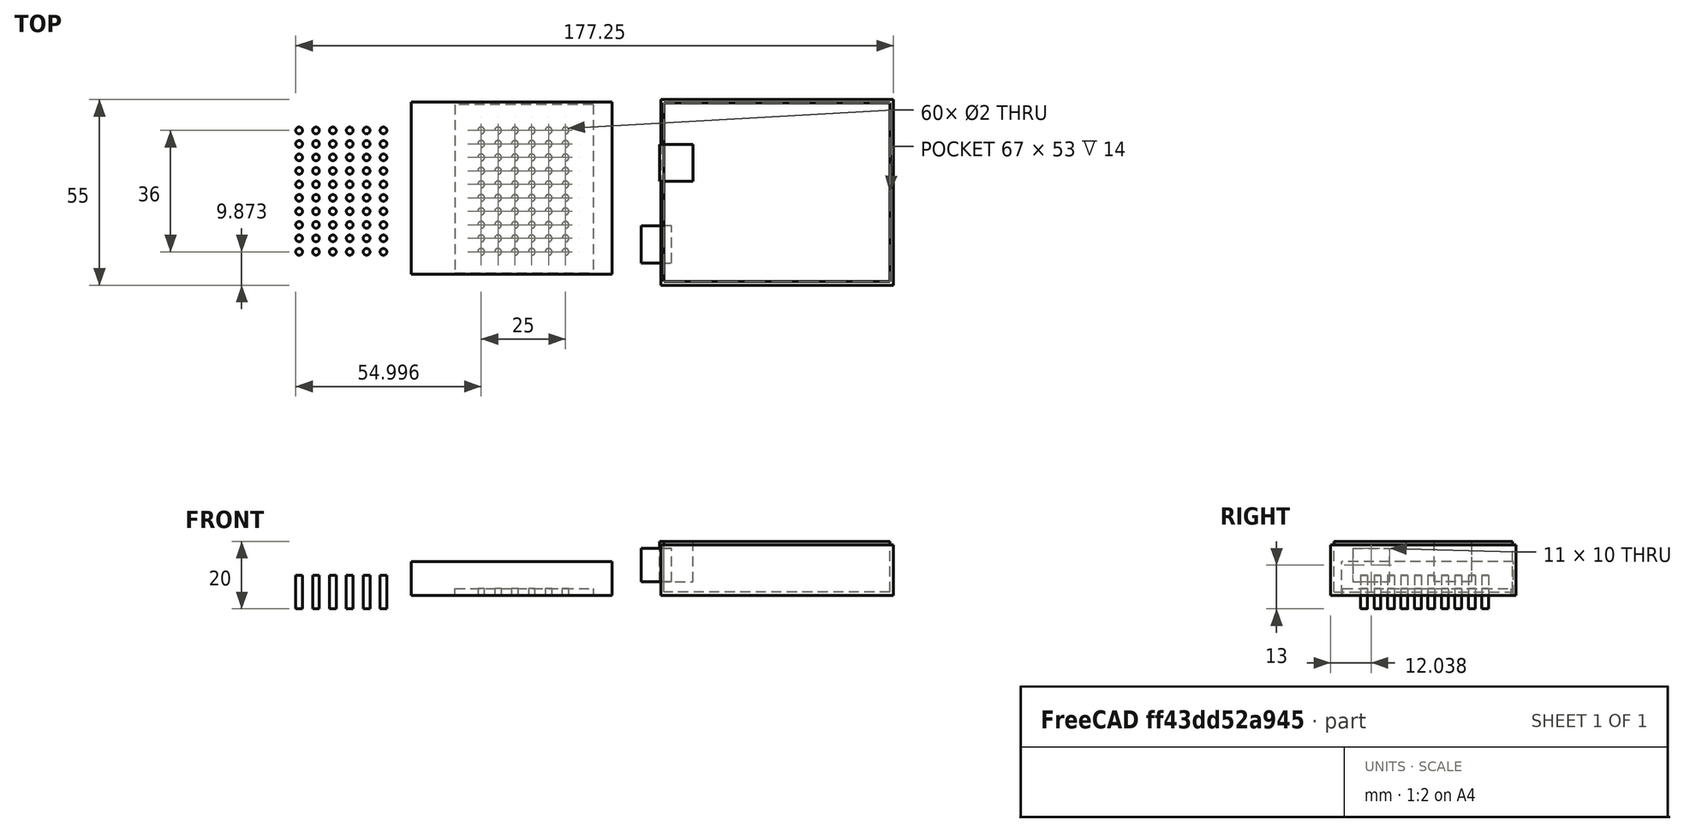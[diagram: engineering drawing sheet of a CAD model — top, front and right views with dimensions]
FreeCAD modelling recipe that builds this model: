
FCSTD DOCUMENT  (FreeCAD 1.0R39109 (Git))
Label: Arduino_component
License: All rights reserved
LicenseURL: https://en.wikipedia.org/wiki/All_rights_reserved
objects: Sketcher::SketchObject×67, PartDesign::Pad×67, PartDesign::Body×67, PartDesign::Boolean×14, Mesh::Feature×1
note: 430 computed .brp shape members not serialized (recipe doc carries the construction recipe); baked Part::Feature solids carry a one-line shape summary decoded from their .brp

FEATURE [Mesh::Feature] arduino
  Placement = pos=(2,0,-5) rot=(0,0,1;0rad)
FEATURE [Sketcher::SketchObject] Sketch
  ArcFitTolerance = 1e-06
  AttachmentSupport = -> [XY_Plane]
  FullyConstrained = false
  MakeInternals = false
  MapMode = 5
  sketch-geometry (4):
    g0: LineSegment StartX=37.3651 StartY=-26.7515 StartZ=0 EndX=-31.6349 EndY=-26.7515 EndZ=0
    g1: LineSegment StartX=-31.6349 StartY=-26.7515 StartZ=0 EndX=-31.6349 EndY=28.2485 EndZ=0
    g2: LineSegment StartX=-31.6349 StartY=28.2485 StartZ=0 EndX=37.3651 EndY=28.2485 EndZ=0
    g3: LineSegment StartX=37.3651 StartY=28.2485 StartZ=0 EndX=37.3651 EndY=-26.7515 EndZ=0
  constraints (10):
    c: Distance(g0) = 69
    c: Horizontal(g0)
    c: Distance(g1) = 55
    c: Coincident(g1,g0)
    c: Vertical(g1)
    c: Distance(g2) = 69
    c: Coincident(g2,g1)
    c: Horizontal(g2)
    c: Coincident(g3,g2)
    c: Coincident(g3,g0)
FEATURE [PartDesign::Pad] Pad
  Direction = (0,0,1)
  Length = 15
  Length2 = 10
  Profile = -> Sketch
  ReferenceAxis = -> Sketch [N_Axis]
  Refine = true
  Suppressed = false
  Type = 0
FEATURE [Sketcher::SketchObject] Sketch001
  ArcFitTolerance = 1e-06
  AttachmentSupport = -> [XY_Plane001]
  FullyConstrained = false
  MakeInternals = false
  MapMode = 5
  sketch-geometry (4):
    g0: LineSegment StartX=6.33937 StartY=-84.733 StartZ=0 EndX=-60.6606 EndY=-84.733 EndZ=0
    g1: LineSegment StartX=-60.6606 StartY=-84.733 StartZ=0 EndX=-60.6606 EndY=-31.733 EndZ=0
    g2: LineSegment StartX=-60.6606 StartY=-31.733 StartZ=0 EndX=6.33937 EndY=-31.733 EndZ=0
    g3: LineSegment StartX=6.33937 StartY=-31.733 StartZ=0 EndX=6.33937 EndY=-84.733 EndZ=0
  constraints (10):
    c: Distance(g0) = 67
    c: Horizontal(g0)
    c: Distance(g1) = 53
    c: Coincident(g1,g0)
    c: Vertical(g1)
    c: Distance(g2) = 67
    c: Coincident(g2,g1)
    c: Horizontal(g2)
    c: Coincident(g3,g2)
    c: Coincident(g3,g0)
FEATURE [PartDesign::Pad] Pad001
  Direction = (0,0,1)
  Length = 15
  Length2 = 10
  Profile = -> Sketch001
  ReferenceAxis = -> Sketch001 [N_Axis]
  Refine = true
  Suppressed = false
  Type = 0
FEATURE [PartDesign::Body] Body001
  AllowCompound = false
  Group = -> [Sketch001,Pad001]
  Origin = -> Origin001
  Placement = pos=(30,59,1) rot=(0,0,1;0rad)
  Tip = -> Pad001
FEATURE [PartDesign::Boolean] Boolean
  BaseFeature = -> Pad
  Group = -> [Body001]
  Refine = true
  Suppressed = false
  Type = 1
  UsePlacement = true
FEATURE [Sketcher::SketchObject] Sketch002
  ArcFitTolerance = 1e-06
  AttachmentSupport = -> [YZ_Plane002]
  FullyConstrained = true
  MakeInternals = false
  MapMode = 5
  Placement = pos=(0,0,0) rot=(0.57735,0.57735,0.57735;2.0944rad)
  sketch-geometry (4):
    g0: LineSegment StartX=11 StartY=0 StartZ=0 EndX=0 EndY=0 EndZ=0
    g1: LineSegment StartX=0 StartY=0 StartZ=0 EndX=0 EndY=12 EndZ=0
    g2: LineSegment StartX=0 StartY=12 StartZ=0 EndX=11 EndY=12 EndZ=0
    g3: LineSegment StartX=11 StartY=12 StartZ=0 EndX=11 EndY=0 EndZ=0
  constraints (11):
    c: Distance(g0) = 11
    c: PointOnObject(g0,g-1)
    c: Coincident(g0,g-1)
    c: Distance(g1) = 12
    c: Coincident(g1,g0)
    c: PointOnObject(g1,g-2)
    c: Distance(g2) = 11
    c: Coincident(g2,g1)
    c: Horizontal(g2)
    c: Coincident(g3,g2)
    c: Coincident(g3,g0)
FEATURE [PartDesign::Pad] Pad002
  Direction = (1,0,0)
  Length = 10
  Length2 = 10
  Placement = pos=(0,0,0) rot=(1,1,1;2.0944rad)
  Profile = -> Sketch002
  ReferenceAxis = -> Sketch002 [N_Axis]
  Refine = true
  Suppressed = false
  Type = 0
FEATURE [PartDesign::Body] Body002
  AllowCompound = false
  Group = -> [Sketch002,Pad002]
  Origin = -> Origin002
  Placement = pos=(-32,4,4) rot=(0,0,1;0rad)
  Tip = -> Pad002
FEATURE [PartDesign::Boolean] Boolean001
  BaseFeature = -> Boolean
  Group = -> [Body002]
  Refine = true
  Suppressed = false
  Type = 1
  UsePlacement = true
FEATURE [Sketcher::SketchObject] Sketch003
  ArcFitTolerance = 1e-06
  AttachmentSupport = -> [XY_Plane003]
  FullyConstrained = false
  MakeInternals = false
  MapMode = 5
  sketch-geometry (4):
    g0: LineSegment StartX=-46.405 StartY=-18.212 StartZ=0 EndX=-37.405 EndY=-18.212 EndZ=0
    g1: LineSegment StartX=-37.405 StartY=-18.212 StartZ=0 EndX=-37.405 EndY=-7.21195 EndZ=0
    g2: LineSegment StartX=-37.405 StartY=-7.21195 StartZ=0 EndX=-46.405 EndY=-7.21195 EndZ=0
    g3: LineSegment StartX=-46.405 StartY=-7.21195 StartZ=0 EndX=-46.405 EndY=-18.212 EndZ=0
  constraints (10):
    c: Distance(g0) = 9
    c: Horizontal(g0)
    c: Distance(g1) = 11
    c: Coincident(g1,g0)
    c: Vertical(g1)
    c: Distance(g2) = 9
    c: Coincident(g2,g1)
    c: Horizontal(g2)
    c: Coincident(g3,g2)
    c: Coincident(g3,g0)
FEATURE [PartDesign::Pad] Pad003
  Direction = (0,0,1)
  Length = 10
  Length2 = 10
  Profile = -> Sketch003
  ReferenceAxis = -> Sketch003 [N_Axis]
  Refine = true
  Suppressed = false
  Type = 0
FEATURE [PartDesign::Body] Body003
  AllowCompound = false
  Group = -> [Sketch003,Pad003]
  Origin = -> Origin003
  Placement = pos=(9,-2,4) rot=(0,0,1;0rad)
  Tip = -> Pad003
FEATURE [PartDesign::Boolean] Boolean002
  BaseFeature = -> Boolean001
  Group = -> [Body003]
  Refine = true
  Suppressed = false
  Type = 1
  UsePlacement = true
FEATURE [PartDesign::Body] Body
  AllowCompound = false
  Group = -> [Sketch,Pad,Boolean,Boolean001,Boolean002]
  Origin = -> Origin
  Tip = -> Boolean002
FEATURE [Sketcher::SketchObject] Sketch004
  ArcFitTolerance = 1e-06
  AttachmentSupport = -> [XY_Plane004]
  FullyConstrained = false
  MakeInternals = false
  MapMode = 5
  sketch-geometry (4):
    g0: LineSegment StartX=-146.689 StartY=-23.1625 StartZ=0 EndX=-46.6885 EndY=-23.1625 EndZ=0
    g1: LineSegment StartX=-46.6885 StartY=-23.1625 StartZ=0 EndX=-46.6885 EndY=26.8375 EndZ=0
    g2: LineSegment StartX=-46.6885 StartY=26.8375 StartZ=0 EndX=-146.689 EndY=26.8375 EndZ=0
    g3: LineSegment StartX=-146.689 StartY=26.8375 StartZ=0 EndX=-146.689 EndY=-23.1625 EndZ=0
  constraints (10):
    c: Distance(g0) = 100
    c: Horizontal(g0)
    c: Distance(g1) = 50
    c: Coincident(g1,g0)
    c: Vertical(g1)
    c: Distance(g2) = 100
    c: Coincident(g2,g1)
    c: Horizontal(g2)
    c: Coincident(g3,g2)
    c: Coincident(g3,g0)
FEATURE [PartDesign::Pad] Pad004
  Direction = (0,0,1)
  Length = 2
  Length2 = 10
  Profile = -> Sketch004
  ReferenceAxis = -> Sketch004 [N_Axis]
  Refine = true
  Suppressed = false
  Type = 0
FEATURE [Sketcher::SketchObject] Sketch005
  ArcFitTolerance = 1e-06
  AttachmentSupport = -> [XY_Plane005]
  FullyConstrained = false
  MakeInternals = false
  MapMode = 5
  sketch-geometry (1):
    g0: Circle CenterX=-36.8843 CenterY=-31.8769 CenterZ=0 NormalX=0 NormalY=0 NormalZ=1 AngleXU=0 Radius=1
  constraints (1):
    c: Diameter(g0) = 2
FEATURE [PartDesign::Pad] Pad005
  Direction = (0,0,1)
  Length = 10
  Length2 = 10
  Profile = -> Sketch005
  ReferenceAxis = -> Sketch005 [N_Axis]
  Refine = true
  Suppressed = false
  Type = 0
FEATURE [PartDesign::Body] Body005
  AllowCompound = false
  Group = -> [Sketch005,Pad005]
  Origin = -> Origin005
  Placement = pos=(-102,15,-4) rot=(0,0,1;0rad)
  Tip = -> Pad005
FEATURE [Sketcher::SketchObject] Sketch006
  ArcFitTolerance = 1e-06
  AttachmentSupport = -> [XY_Plane006]
  FullyConstrained = false
  MakeInternals = false
  MapMode = 5
  sketch-geometry (1):
    g0: Circle CenterX=-36.8843 CenterY=-31.8769 CenterZ=0 NormalX=0 NormalY=0 NormalZ=1 AngleXU=0 Radius=1
  constraints (1):
    c: Diameter(g0) = 2
FEATURE [PartDesign::Pad] Pad006
  Direction = (0,0,1)
  Length = 10
  Length2 = 10
  Profile = -> Sketch006
  ReferenceAxis = -> Sketch006 [N_Axis]
  Refine = true
  Suppressed = false
  Type = 0
FEATURE [PartDesign::Body] Body006
  AllowCompound = false
  Group = -> [Sketch006,Pad006]
  Origin = -> Origin006
  Placement = pos=(-97,15,-4) rot=(0,0,1;0rad)
  Tip = -> Pad006
FEATURE [Sketcher::SketchObject] Sketch007
  ArcFitTolerance = 1e-06
  AttachmentSupport = -> [XY_Plane007]
  FullyConstrained = false
  MakeInternals = false
  MapMode = 5
  sketch-geometry (1):
    g0: Circle CenterX=-36.8843 CenterY=-31.8769 CenterZ=0 NormalX=0 NormalY=0 NormalZ=1 AngleXU=0 Radius=1
  constraints (1):
    c: Diameter(g0) = 2
FEATURE [PartDesign::Pad] Pad007
  Direction = (0,0,1)
  Length = 10
  Length2 = 10
  Profile = -> Sketch007
  ReferenceAxis = -> Sketch007 [N_Axis]
  Refine = true
  Suppressed = false
  Type = 0
FEATURE [PartDesign::Body] Body007
  AllowCompound = false
  Group = -> [Sketch007,Pad007]
  Origin = -> Origin007
  Placement = pos=(-92,15,-4) rot=(0,0,1;0rad)
  Tip = -> Pad007
FEATURE [Sketcher::SketchObject] Sketch008
  ArcFitTolerance = 1e-06
  AttachmentSupport = -> [XY_Plane008]
  FullyConstrained = false
  MakeInternals = false
  MapMode = 5
  sketch-geometry (1):
    g0: Circle CenterX=-36.8843 CenterY=-31.8769 CenterZ=0 NormalX=0 NormalY=0 NormalZ=1 AngleXU=0 Radius=1
  constraints (1):
    c: Diameter(g0) = 2
FEATURE [PartDesign::Pad] Pad008
  Direction = (0,0,1)
  Length = 10
  Length2 = 10
  Profile = -> Sketch008
  ReferenceAxis = -> Sketch008 [N_Axis]
  Refine = true
  Suppressed = false
  Type = 0
FEATURE [PartDesign::Body] Body008
  AllowCompound = false
  Group = -> [Sketch008,Pad008]
  Origin = -> Origin008
  Placement = pos=(-87,15,-4) rot=(0,0,1;0rad)
  Tip = -> Pad008
FEATURE [Sketcher::SketchObject] Sketch009
  ArcFitTolerance = 1e-06
  AttachmentSupport = -> [XY_Plane009]
  FullyConstrained = false
  MakeInternals = false
  MapMode = 5
  sketch-geometry (1):
    g0: Circle CenterX=-36.8843 CenterY=-31.8769 CenterZ=0 NormalX=0 NormalY=0 NormalZ=1 AngleXU=0 Radius=1
  constraints (1):
    c: Diameter(g0) = 2
FEATURE [PartDesign::Pad] Pad009
  Direction = (0,0,1)
  Length = 10
  Length2 = 10
  Profile = -> Sketch009
  ReferenceAxis = -> Sketch009 [N_Axis]
  Refine = true
  Suppressed = false
  Type = 0
FEATURE [PartDesign::Body] Body009
  AllowCompound = false
  Group = -> [Sketch009,Pad009]
  Origin = -> Origin009
  Placement = pos=(-82,15,-4) rot=(0,0,1;0rad)
  Tip = -> Pad009
FEATURE [Sketcher::SketchObject] Sketch010
  ArcFitTolerance = 1e-06
  AttachmentSupport = -> [XY_Plane010]
  FullyConstrained = false
  MakeInternals = false
  MapMode = 5
  sketch-geometry (1):
    g0: Circle CenterX=-36.8843 CenterY=-31.8769 CenterZ=0 NormalX=0 NormalY=0 NormalZ=1 AngleXU=0 Radius=1
  constraints (1):
    c: Diameter(g0) = 2
FEATURE [PartDesign::Pad] Pad010
  Direction = (0,0,1)
  Length = 10
  Length2 = 10
  Profile = -> Sketch010
  ReferenceAxis = -> Sketch010 [N_Axis]
  Refine = true
  Suppressed = false
  Type = 0
FEATURE [PartDesign::Body] Body010
  AllowCompound = false
  Group = -> [Sketch010,Pad010]
  Origin = -> Origin010
  Placement = pos=(-77,15,-4) rot=(0,0,1;0rad)
  Tip = -> Pad010
FEATURE [PartDesign::Boolean] Boolean003
  BaseFeature = -> Pad004
  Group = -> [Body005,Body006,Body007,Body008,Body009]
  Refine = true
  Suppressed = false
  Type = 1
  UsePlacement = true
FEATURE [Sketcher::SketchObject] Sketch011
  ArcFitTolerance = 1e-06
  AttachmentSupport = -> [XY_Plane011]
  FullyConstrained = false
  MakeInternals = false
  MapMode = 5
  sketch-geometry (1):
    g0: Circle CenterX=-36.8843 CenterY=-31.8769 CenterZ=0 NormalX=0 NormalY=0 NormalZ=1 AngleXU=0 Radius=1
  constraints (1):
    c: Diameter(g0) = 2
FEATURE [PartDesign::Pad] Pad011
  Direction = (0,0,1)
  Length = 10
  Length2 = 10
  Profile = -> Sketch011
  ReferenceAxis = -> Sketch011 [N_Axis]
  Refine = true
  Suppressed = false
  Type = 0
FEATURE [PartDesign::Body] Body011
  AllowCompound = false
  Group = -> [Sketch011,Pad011]
  Origin = -> Origin011
  Placement = pos=(-102,19,-4) rot=(0,0,1;0rad)
  Tip = -> Pad011
FEATURE [Sketcher::SketchObject] Sketch012
  ArcFitTolerance = 1e-06
  AttachmentSupport = -> [XY_Plane012]
  FullyConstrained = false
  MakeInternals = false
  MapMode = 5
  sketch-geometry (1):
    g0: Circle CenterX=-36.8843 CenterY=-31.8769 CenterZ=0 NormalX=0 NormalY=0 NormalZ=1 AngleXU=0 Radius=1
  constraints (1):
    c: Diameter(g0) = 2
FEATURE [PartDesign::Pad] Pad012
  Direction = (0,0,1)
  Length = 10
  Length2 = 10
  Profile = -> Sketch012
  ReferenceAxis = -> Sketch012 [N_Axis]
  Refine = true
  Suppressed = false
  Type = 0
FEATURE [PartDesign::Body] Body012
  AllowCompound = false
  Group = -> [Sketch012,Pad012]
  Origin = -> Origin012
  Placement = pos=(-97,19,-4) rot=(0,0,1;0rad)
  Tip = -> Pad012
FEATURE [Sketcher::SketchObject] Sketch013
  ArcFitTolerance = 1e-06
  AttachmentSupport = -> [XY_Plane013]
  FullyConstrained = false
  MakeInternals = false
  MapMode = 5
  sketch-geometry (1):
    g0: Circle CenterX=-36.8843 CenterY=-31.8769 CenterZ=0 NormalX=0 NormalY=0 NormalZ=1 AngleXU=0 Radius=1
  constraints (1):
    c: Diameter(g0) = 2
FEATURE [PartDesign::Pad] Pad013
  Direction = (0,0,1)
  Length = 10
  Length2 = 10
  Profile = -> Sketch013
  ReferenceAxis = -> Sketch013 [N_Axis]
  Refine = true
  Suppressed = false
  Type = 0
FEATURE [PartDesign::Body] Body013
  AllowCompound = false
  Group = -> [Sketch013,Pad013]
  Origin = -> Origin013
  Placement = pos=(-92,19,-4) rot=(0,0,1;0rad)
  Tip = -> Pad013
FEATURE [Sketcher::SketchObject] Sketch014
  ArcFitTolerance = 1e-06
  AttachmentSupport = -> [XY_Plane014]
  FullyConstrained = false
  MakeInternals = false
  MapMode = 5
  sketch-geometry (1):
    g0: Circle CenterX=-36.8843 CenterY=-31.8769 CenterZ=0 NormalX=0 NormalY=0 NormalZ=1 AngleXU=0 Radius=1
  constraints (1):
    c: Diameter(g0) = 2
FEATURE [PartDesign::Pad] Pad014
  Direction = (0,0,1)
  Length = 10
  Length2 = 10
  Profile = -> Sketch014
  ReferenceAxis = -> Sketch014 [N_Axis]
  Refine = true
  Suppressed = false
  Type = 0
FEATURE [PartDesign::Body] Body014
  AllowCompound = false
  Group = -> [Sketch014,Pad014]
  Origin = -> Origin014
  Placement = pos=(-87,19,-4) rot=(0,0,1;0rad)
  Tip = -> Pad014
FEATURE [Sketcher::SketchObject] Sketch015
  ArcFitTolerance = 1e-06
  AttachmentSupport = -> [XY_Plane015]
  FullyConstrained = false
  MakeInternals = false
  MapMode = 5
  sketch-geometry (1):
    g0: Circle CenterX=-36.8843 CenterY=-31.8769 CenterZ=0 NormalX=0 NormalY=0 NormalZ=1 AngleXU=0 Radius=1
  constraints (1):
    c: Diameter(g0) = 2
FEATURE [PartDesign::Pad] Pad015
  Direction = (0,0,1)
  Length = 10
  Length2 = 10
  Profile = -> Sketch015
  ReferenceAxis = -> Sketch015 [N_Axis]
  Refine = true
  Suppressed = false
  Type = 0
FEATURE [PartDesign::Body] Body015
  AllowCompound = false
  Group = -> [Sketch015,Pad015]
  Origin = -> Origin015
  Placement = pos=(-82,19,-4) rot=(0,0,1;0rad)
  Tip = -> Pad015
FEATURE [Sketcher::SketchObject] Sketch016
  ArcFitTolerance = 1e-06
  AttachmentSupport = -> [XY_Plane016]
  FullyConstrained = false
  MakeInternals = false
  MapMode = 5
  sketch-geometry (1):
    g0: Circle CenterX=-36.8843 CenterY=-31.8769 CenterZ=0 NormalX=0 NormalY=0 NormalZ=1 AngleXU=0 Radius=1
  constraints (1):
    c: Diameter(g0) = 2
FEATURE [PartDesign::Pad] Pad016
  Direction = (0,0,1)
  Length = 10
  Length2 = 10
  Profile = -> Sketch016
  ReferenceAxis = -> Sketch016 [N_Axis]
  Refine = true
  Suppressed = false
  Type = 0
FEATURE [PartDesign::Body] Body016
  AllowCompound = false
  Group = -> [Sketch016,Pad016]
  Origin = -> Origin016
  Placement = pos=(-77,19,-4) rot=(0,0,1;0rad)
  Tip = -> Pad016
FEATURE [Sketcher::SketchObject] Sketch017
  ArcFitTolerance = 1e-06
  AttachmentSupport = -> [XY_Plane017]
  FullyConstrained = false
  MakeInternals = false
  MapMode = 5
  sketch-geometry (1):
    g0: Circle CenterX=-36.8843 CenterY=-31.8769 CenterZ=0 NormalX=0 NormalY=0 NormalZ=1 AngleXU=0 Radius=1
  constraints (1):
    c: Diameter(g0) = 2
FEATURE [PartDesign::Pad] Pad017
  Direction = (0,0,1)
  Length = 10
  Length2 = 10
  Profile = -> Sketch017
  ReferenceAxis = -> Sketch017 [N_Axis]
  Refine = true
  Suppressed = false
  Type = 0
FEATURE [PartDesign::Body] Body017
  AllowCompound = false
  Group = -> [Sketch017,Pad017]
  Origin = -> Origin017
  Placement = pos=(-77,15,-4) rot=(0,0,1;0rad)
  Tip = -> Pad017
FEATURE [PartDesign::Boolean] Boolean004
  BaseFeature = -> Boolean003
  Group = -> [Body011,Body012,Body013,Body014,Body015,Body016,Body017,Body010]
  Refine = true
  Suppressed = false
  Type = 1
  UsePlacement = true
FEATURE [Sketcher::SketchObject] Sketch018
  ArcFitTolerance = 1e-06
  AttachmentSupport = -> [XY_Plane018]
  FullyConstrained = false
  MakeInternals = false
  MapMode = 5
  sketch-geometry (1):
    g0: Circle CenterX=-36.8843 CenterY=-31.8769 CenterZ=0 NormalX=0 NormalY=0 NormalZ=1 AngleXU=0 Radius=1
  constraints (1):
    c: Diameter(g0) = 2
FEATURE [PartDesign::Pad] Pad018
  Direction = (0,0,1)
  Length = 10
  Length2 = 10
  Profile = -> Sketch018
  ReferenceAxis = -> Sketch018 [N_Axis]
  Refine = true
  Suppressed = false
  Type = 0
FEATURE [PartDesign::Body] Body018
  AllowCompound = false
  Group = -> [Sketch018,Pad018]
  Origin = -> Origin018
  Placement = pos=(-102,23,-4) rot=(0,0,1;0rad)
  Tip = -> Pad018
FEATURE [Sketcher::SketchObject] Sketch019
  ArcFitTolerance = 1e-06
  AttachmentSupport = -> [XY_Plane019]
  FullyConstrained = false
  MakeInternals = false
  MapMode = 5
  sketch-geometry (1):
    g0: Circle CenterX=-36.8843 CenterY=-31.8769 CenterZ=0 NormalX=0 NormalY=0 NormalZ=1 AngleXU=0 Radius=1
  constraints (1):
    c: Diameter(g0) = 2
FEATURE [PartDesign::Pad] Pad019
  Direction = (0,0,1)
  Length = 10
  Length2 = 10
  Profile = -> Sketch019
  ReferenceAxis = -> Sketch019 [N_Axis]
  Refine = true
  Suppressed = false
  Type = 0
FEATURE [PartDesign::Body] Body019
  AllowCompound = false
  Group = -> [Sketch019,Pad019]
  Origin = -> Origin019
  Placement = pos=(-97,23,-4) rot=(0,0,1;0rad)
  Tip = -> Pad019
FEATURE [Sketcher::SketchObject] Sketch020
  ArcFitTolerance = 1e-06
  AttachmentSupport = -> [XY_Plane020]
  FullyConstrained = false
  MakeInternals = false
  MapMode = 5
  sketch-geometry (1):
    g0: Circle CenterX=-36.8843 CenterY=-31.8769 CenterZ=0 NormalX=0 NormalY=0 NormalZ=1 AngleXU=0 Radius=1
  constraints (1):
    c: Diameter(g0) = 2
FEATURE [PartDesign::Pad] Pad020
  Direction = (0,0,1)
  Length = 10
  Length2 = 10
  Profile = -> Sketch020
  ReferenceAxis = -> Sketch020 [N_Axis]
  Refine = true
  Suppressed = false
  Type = 0
FEATURE [PartDesign::Body] Body020
  AllowCompound = false
  Group = -> [Sketch020,Pad020]
  Origin = -> Origin020
  Placement = pos=(-92,23,-4) rot=(0,0,1;0rad)
  Tip = -> Pad020
FEATURE [Sketcher::SketchObject] Sketch021
  ArcFitTolerance = 1e-06
  AttachmentSupport = -> [XY_Plane021]
  FullyConstrained = false
  MakeInternals = false
  MapMode = 5
  sketch-geometry (1):
    g0: Circle CenterX=-36.8843 CenterY=-31.8769 CenterZ=0 NormalX=0 NormalY=0 NormalZ=1 AngleXU=0 Radius=1
  constraints (1):
    c: Diameter(g0) = 2
FEATURE [PartDesign::Pad] Pad021
  Direction = (0,0,1)
  Length = 10
  Length2 = 10
  Profile = -> Sketch021
  ReferenceAxis = -> Sketch021 [N_Axis]
  Refine = true
  Suppressed = false
  Type = 0
FEATURE [PartDesign::Body] Body021
  AllowCompound = false
  Group = -> [Sketch021,Pad021]
  Origin = -> Origin021
  Placement = pos=(-87,23,-4) rot=(0,0,1;0rad)
  Tip = -> Pad021
FEATURE [Sketcher::SketchObject] Sketch022
  ArcFitTolerance = 1e-06
  AttachmentSupport = -> [XY_Plane022]
  FullyConstrained = false
  MakeInternals = false
  MapMode = 5
  sketch-geometry (1):
    g0: Circle CenterX=-36.8843 CenterY=-31.8769 CenterZ=0 NormalX=0 NormalY=0 NormalZ=1 AngleXU=0 Radius=1
  constraints (1):
    c: Diameter(g0) = 2
FEATURE [PartDesign::Pad] Pad022
  Direction = (0,0,1)
  Length = 10
  Length2 = 10
  Profile = -> Sketch022
  ReferenceAxis = -> Sketch022 [N_Axis]
  Refine = true
  Suppressed = false
  Type = 0
FEATURE [PartDesign::Body] Body022
  AllowCompound = false
  Group = -> [Sketch022,Pad022]
  Origin = -> Origin022
  Placement = pos=(-82,23,-4) rot=(0,0,1;0rad)
  Tip = -> Pad022
FEATURE [Sketcher::SketchObject] Sketch023
  ArcFitTolerance = 1e-06
  AttachmentSupport = -> [XY_Plane023]
  FullyConstrained = false
  MakeInternals = false
  MapMode = 5
  sketch-geometry (1):
    g0: Circle CenterX=-36.8843 CenterY=-31.8769 CenterZ=0 NormalX=0 NormalY=0 NormalZ=1 AngleXU=0 Radius=1
  constraints (1):
    c: Diameter(g0) = 2
FEATURE [PartDesign::Pad] Pad023
  Direction = (0,0,1)
  Length = 10
  Length2 = 10
  Profile = -> Sketch023
  ReferenceAxis = -> Sketch023 [N_Axis]
  Refine = true
  Suppressed = false
  Type = 0
FEATURE [PartDesign::Body] Body023
  AllowCompound = false
  Group = -> [Sketch023,Pad023]
  Origin = -> Origin023
  Placement = pos=(-77,23,-4) rot=(0,0,1;0rad)
  Tip = -> Pad023
FEATURE [PartDesign::Boolean] Boolean005
  BaseFeature = -> Boolean004
  Group = -> [Body018,Body019,Body020,Body021,Body022,Body023]
  Refine = true
  Suppressed = false
  Type = 1
  UsePlacement = true
FEATURE [Sketcher::SketchObject] Sketch024
  ArcFitTolerance = 1e-06
  AttachmentSupport = -> [XY_Plane024]
  FullyConstrained = false
  MakeInternals = false
  MapMode = 5
  sketch-geometry (1):
    g0: Circle CenterX=-36.8843 CenterY=-31.8769 CenterZ=0 NormalX=0 NormalY=0 NormalZ=1 AngleXU=0 Radius=1
  constraints (1):
    c: Diameter(g0) = 2
FEATURE [PartDesign::Pad] Pad024
  Direction = (0,0,1)
  Length = 10
  Length2 = 10
  Profile = -> Sketch024
  ReferenceAxis = -> Sketch024 [N_Axis]
  Refine = true
  Suppressed = false
  Type = 0
FEATURE [PartDesign::Body] Body024
  AllowCompound = false
  Group = -> [Sketch024,Pad024]
  Origin = -> Origin024
  Placement = pos=(-102,27,-4) rot=(0,0,1;0rad)
  Tip = -> Pad024
FEATURE [Sketcher::SketchObject] Sketch025
  ArcFitTolerance = 1e-06
  AttachmentSupport = -> [XY_Plane025]
  FullyConstrained = false
  MakeInternals = false
  MapMode = 5
  sketch-geometry (1):
    g0: Circle CenterX=-36.8843 CenterY=-31.8769 CenterZ=0 NormalX=0 NormalY=0 NormalZ=1 AngleXU=0 Radius=1
  constraints (1):
    c: Diameter(g0) = 2
FEATURE [PartDesign::Pad] Pad025
  Direction = (0,0,1)
  Length = 10
  Length2 = 10
  Profile = -> Sketch025
  ReferenceAxis = -> Sketch025 [N_Axis]
  Refine = true
  Suppressed = false
  Type = 0
FEATURE [PartDesign::Body] Body025
  AllowCompound = false
  Group = -> [Sketch025,Pad025]
  Origin = -> Origin025
  Placement = pos=(-97,27,-4) rot=(0,0,1;0rad)
  Tip = -> Pad025
FEATURE [Sketcher::SketchObject] Sketch026
  ArcFitTolerance = 1e-06
  AttachmentSupport = -> [XY_Plane026]
  FullyConstrained = false
  MakeInternals = false
  MapMode = 5
  sketch-geometry (1):
    g0: Circle CenterX=-36.8843 CenterY=-31.8769 CenterZ=0 NormalX=0 NormalY=0 NormalZ=1 AngleXU=0 Radius=1
  constraints (1):
    c: Diameter(g0) = 2
FEATURE [PartDesign::Pad] Pad026
  Direction = (0,0,1)
  Length = 10
  Length2 = 10
  Profile = -> Sketch026
  ReferenceAxis = -> Sketch026 [N_Axis]
  Refine = true
  Suppressed = false
  Type = 0
FEATURE [PartDesign::Body] Body026
  AllowCompound = false
  Group = -> [Sketch026,Pad026]
  Origin = -> Origin026
  Placement = pos=(-92,27,-4) rot=(0,0,1;0rad)
  Tip = -> Pad026
FEATURE [Sketcher::SketchObject] Sketch027
  ArcFitTolerance = 1e-06
  AttachmentSupport = -> [XY_Plane027]
  FullyConstrained = false
  MakeInternals = false
  MapMode = 5
  sketch-geometry (1):
    g0: Circle CenterX=-36.8843 CenterY=-31.8769 CenterZ=0 NormalX=0 NormalY=0 NormalZ=1 AngleXU=0 Radius=1
  constraints (1):
    c: Diameter(g0) = 2
FEATURE [PartDesign::Pad] Pad027
  Direction = (0,0,1)
  Length = 10
  Length2 = 10
  Profile = -> Sketch027
  ReferenceAxis = -> Sketch027 [N_Axis]
  Refine = true
  Suppressed = false
  Type = 0
FEATURE [PartDesign::Body] Body027
  AllowCompound = false
  Group = -> [Sketch027,Pad027]
  Origin = -> Origin027
  Placement = pos=(-87,27,-4) rot=(0,0,1;0rad)
  Tip = -> Pad027
FEATURE [Sketcher::SketchObject] Sketch028
  ArcFitTolerance = 1e-06
  AttachmentSupport = -> [XY_Plane028]
  FullyConstrained = false
  MakeInternals = false
  MapMode = 5
  sketch-geometry (1):
    g0: Circle CenterX=-36.8843 CenterY=-31.8769 CenterZ=0 NormalX=0 NormalY=0 NormalZ=1 AngleXU=0 Radius=1
  constraints (1):
    c: Diameter(g0) = 2
FEATURE [PartDesign::Pad] Pad028
  Direction = (0,0,1)
  Length = 10
  Length2 = 10
  Profile = -> Sketch028
  ReferenceAxis = -> Sketch028 [N_Axis]
  Refine = true
  Suppressed = false
  Type = 0
FEATURE [PartDesign::Body] Body028
  AllowCompound = false
  Group = -> [Sketch028,Pad028]
  Origin = -> Origin028
  Placement = pos=(-82,27,-4) rot=(0,0,1;0rad)
  Tip = -> Pad028
FEATURE [Sketcher::SketchObject] Sketch029
  ArcFitTolerance = 1e-06
  AttachmentSupport = -> [XY_Plane029]
  FullyConstrained = false
  MakeInternals = false
  MapMode = 5
  sketch-geometry (1):
    g0: Circle CenterX=-36.8843 CenterY=-31.8769 CenterZ=0 NormalX=0 NormalY=0 NormalZ=1 AngleXU=0 Radius=1
  constraints (1):
    c: Diameter(g0) = 2
FEATURE [PartDesign::Pad] Pad029
  Direction = (0,0,1)
  Length = 10
  Length2 = 10
  Profile = -> Sketch029
  ReferenceAxis = -> Sketch029 [N_Axis]
  Refine = true
  Suppressed = false
  Type = 0
FEATURE [PartDesign::Body] Body029
  AllowCompound = false
  Group = -> [Sketch029,Pad029]
  Origin = -> Origin029
  Placement = pos=(-77,27,-4) rot=(0,0,1;0rad)
  Tip = -> Pad029
FEATURE [PartDesign::Boolean] Boolean006
  BaseFeature = -> Boolean005
  Group = -> [Body024,Body025,Body026,Body027,Body028,Body029]
  Refine = true
  Suppressed = false
  Type = 1
  UsePlacement = true
FEATURE [Sketcher::SketchObject] Sketch030
  ArcFitTolerance = 1e-06
  AttachmentSupport = -> [XY_Plane030]
  FullyConstrained = false
  MakeInternals = false
  MapMode = 5
  sketch-geometry (1):
    g0: Circle CenterX=-36.8843 CenterY=-31.8769 CenterZ=0 NormalX=0 NormalY=0 NormalZ=1 AngleXU=0 Radius=1
  constraints (1):
    c: Diameter(g0) = 2
FEATURE [PartDesign::Pad] Pad030
  Direction = (0,0,1)
  Length = 10
  Length2 = 10
  Profile = -> Sketch030
  ReferenceAxis = -> Sketch030 [N_Axis]
  Refine = true
  Suppressed = false
  Type = 0
FEATURE [PartDesign::Body] Body030
  AllowCompound = false
  Group = -> [Sketch030,Pad030]
  Origin = -> Origin030
  Placement = pos=(-102,31,-4) rot=(0,0,1;0rad)
  Tip = -> Pad030
FEATURE [Sketcher::SketchObject] Sketch031
  ArcFitTolerance = 1e-06
  AttachmentSupport = -> [XY_Plane031]
  FullyConstrained = false
  MakeInternals = false
  MapMode = 5
  sketch-geometry (1):
    g0: Circle CenterX=-36.8843 CenterY=-31.8769 CenterZ=0 NormalX=0 NormalY=0 NormalZ=1 AngleXU=0 Radius=1
  constraints (1):
    c: Diameter(g0) = 2
FEATURE [PartDesign::Pad] Pad031
  Direction = (0,0,1)
  Length = 10
  Length2 = 10
  Profile = -> Sketch031
  ReferenceAxis = -> Sketch031 [N_Axis]
  Refine = true
  Suppressed = false
  Type = 0
FEATURE [PartDesign::Body] Body031
  AllowCompound = false
  Group = -> [Sketch031,Pad031]
  Origin = -> Origin031
  Placement = pos=(-97,31,-4) rot=(0,0,1;0rad)
  Tip = -> Pad031
FEATURE [Sketcher::SketchObject] Sketch032
  ArcFitTolerance = 1e-06
  AttachmentSupport = -> [XY_Plane032]
  FullyConstrained = false
  MakeInternals = false
  MapMode = 5
  sketch-geometry (1):
    g0: Circle CenterX=-36.8843 CenterY=-31.8769 CenterZ=0 NormalX=0 NormalY=0 NormalZ=1 AngleXU=0 Radius=1
  constraints (1):
    c: Diameter(g0) = 2
FEATURE [PartDesign::Pad] Pad032
  Direction = (0,0,1)
  Length = 10
  Length2 = 10
  Profile = -> Sketch032
  ReferenceAxis = -> Sketch032 [N_Axis]
  Refine = true
  Suppressed = false
  Type = 0
FEATURE [PartDesign::Body] Body032
  AllowCompound = false
  Group = -> [Sketch032,Pad032]
  Origin = -> Origin032
  Placement = pos=(-92,31,-4) rot=(0,0,1;0rad)
  Tip = -> Pad032
FEATURE [Sketcher::SketchObject] Sketch033
  ArcFitTolerance = 1e-06
  AttachmentSupport = -> [XY_Plane033]
  FullyConstrained = false
  MakeInternals = false
  MapMode = 5
  sketch-geometry (1):
    g0: Circle CenterX=-36.8843 CenterY=-31.8769 CenterZ=0 NormalX=0 NormalY=0 NormalZ=1 AngleXU=0 Radius=1
  constraints (1):
    c: Diameter(g0) = 2
FEATURE [PartDesign::Pad] Pad033
  Direction = (0,0,1)
  Length = 10
  Length2 = 10
  Profile = -> Sketch033
  ReferenceAxis = -> Sketch033 [N_Axis]
  Refine = true
  Suppressed = false
  Type = 0
FEATURE [PartDesign::Body] Body033
  AllowCompound = false
  Group = -> [Sketch033,Pad033]
  Origin = -> Origin033
  Placement = pos=(-87,31,-4) rot=(0,0,1;0rad)
  Tip = -> Pad033
FEATURE [Sketcher::SketchObject] Sketch034
  ArcFitTolerance = 1e-06
  AttachmentSupport = -> [XY_Plane034]
  FullyConstrained = false
  MakeInternals = false
  MapMode = 5
  sketch-geometry (1):
    g0: Circle CenterX=-36.8843 CenterY=-31.8769 CenterZ=0 NormalX=0 NormalY=0 NormalZ=1 AngleXU=0 Radius=1
  constraints (1):
    c: Diameter(g0) = 2
FEATURE [PartDesign::Pad] Pad034
  Direction = (0,0,1)
  Length = 10
  Length2 = 10
  Profile = -> Sketch034
  ReferenceAxis = -> Sketch034 [N_Axis]
  Refine = true
  Suppressed = false
  Type = 0
FEATURE [PartDesign::Body] Body034
  AllowCompound = false
  Group = -> [Sketch034,Pad034]
  Origin = -> Origin034
  Placement = pos=(-82,31,-4) rot=(0,0,1;0rad)
  Tip = -> Pad034
FEATURE [Sketcher::SketchObject] Sketch035
  ArcFitTolerance = 1e-06
  AttachmentSupport = -> [XY_Plane035]
  FullyConstrained = false
  MakeInternals = false
  MapMode = 5
  sketch-geometry (1):
    g0: Circle CenterX=-36.8843 CenterY=-31.8769 CenterZ=0 NormalX=0 NormalY=0 NormalZ=1 AngleXU=0 Radius=1
  constraints (1):
    c: Diameter(g0) = 2
FEATURE [PartDesign::Pad] Pad035
  Direction = (0,0,1)
  Length = 10
  Length2 = 10
  Profile = -> Sketch035
  ReferenceAxis = -> Sketch035 [N_Axis]
  Refine = true
  Suppressed = false
  Type = 0
FEATURE [PartDesign::Body] Body035
  AllowCompound = false
  Group = -> [Sketch035,Pad035]
  Origin = -> Origin035
  Placement = pos=(-77,31,-4) rot=(0,0,1;0rad)
  Tip = -> Pad035
FEATURE [PartDesign::Boolean] Boolean007
  BaseFeature = -> Boolean006
  Group = -> [Body030,Body031,Body032,Body033,Body034,Body035]
  Refine = true
  Suppressed = false
  Type = 1
  UsePlacement = true
FEATURE [Sketcher::SketchObject] Sketch036
  ArcFitTolerance = 1e-06
  AttachmentSupport = -> [XY_Plane036]
  FullyConstrained = false
  MakeInternals = false
  MapMode = 5
  sketch-geometry (1):
    g0: Circle CenterX=-36.8843 CenterY=-31.8769 CenterZ=0 NormalX=0 NormalY=0 NormalZ=1 AngleXU=0 Radius=1
  constraints (1):
    c: Diameter(g0) = 2
FEATURE [PartDesign::Pad] Pad036
  Direction = (0,0,1)
  Length = 10
  Length2 = 10
  Profile = -> Sketch036
  ReferenceAxis = -> Sketch036 [N_Axis]
  Refine = true
  Suppressed = false
  Type = 0
FEATURE [PartDesign::Body] Body036
  AllowCompound = false
  Group = -> [Sketch036,Pad036]
  Origin = -> Origin036
  Placement = pos=(-102,35,-4) rot=(0,0,1;0rad)
  Tip = -> Pad036
FEATURE [Sketcher::SketchObject] Sketch037
  ArcFitTolerance = 1e-06
  AttachmentSupport = -> [XY_Plane037]
  FullyConstrained = false
  MakeInternals = false
  MapMode = 5
  sketch-geometry (1):
    g0: Circle CenterX=-36.8843 CenterY=-31.8769 CenterZ=0 NormalX=0 NormalY=0 NormalZ=1 AngleXU=0 Radius=1
  constraints (1):
    c: Diameter(g0) = 2
FEATURE [PartDesign::Pad] Pad037
  Direction = (0,0,1)
  Length = 10
  Length2 = 10
  Profile = -> Sketch037
  ReferenceAxis = -> Sketch037 [N_Axis]
  Refine = true
  Suppressed = false
  Type = 0
FEATURE [PartDesign::Body] Body037
  AllowCompound = false
  Group = -> [Sketch037,Pad037]
  Origin = -> Origin037
  Placement = pos=(-97,35,-4) rot=(0,0,1;0rad)
  Tip = -> Pad037
FEATURE [Sketcher::SketchObject] Sketch038
  ArcFitTolerance = 1e-06
  AttachmentSupport = -> [XY_Plane038]
  FullyConstrained = false
  MakeInternals = false
  MapMode = 5
  sketch-geometry (1):
    g0: Circle CenterX=-36.8843 CenterY=-31.8769 CenterZ=0 NormalX=0 NormalY=0 NormalZ=1 AngleXU=0 Radius=1
  constraints (1):
    c: Diameter(g0) = 2
FEATURE [PartDesign::Pad] Pad038
  Direction = (0,0,1)
  Length = 10
  Length2 = 10
  Profile = -> Sketch038
  ReferenceAxis = -> Sketch038 [N_Axis]
  Refine = true
  Suppressed = false
  Type = 0
FEATURE [PartDesign::Body] Body038
  AllowCompound = false
  Group = -> [Sketch038,Pad038]
  Origin = -> Origin038
  Placement = pos=(-92,35,-4) rot=(0,0,1;0rad)
  Tip = -> Pad038
FEATURE [Sketcher::SketchObject] Sketch039
  ArcFitTolerance = 1e-06
  AttachmentSupport = -> [XY_Plane039]
  FullyConstrained = false
  MakeInternals = false
  MapMode = 5
  sketch-geometry (1):
    g0: Circle CenterX=-36.8843 CenterY=-31.8769 CenterZ=0 NormalX=0 NormalY=0 NormalZ=1 AngleXU=0 Radius=1
  constraints (1):
    c: Diameter(g0) = 2
FEATURE [PartDesign::Pad] Pad039
  Direction = (0,0,1)
  Length = 10
  Length2 = 10
  Profile = -> Sketch039
  ReferenceAxis = -> Sketch039 [N_Axis]
  Refine = true
  Suppressed = false
  Type = 0
FEATURE [PartDesign::Body] Body039
  AllowCompound = false
  Group = -> [Sketch039,Pad039]
  Origin = -> Origin039
  Placement = pos=(-87,35,-4) rot=(0,0,1;0rad)
  Tip = -> Pad039
FEATURE [Sketcher::SketchObject] Sketch040
  ArcFitTolerance = 1e-06
  AttachmentSupport = -> [XY_Plane040]
  FullyConstrained = false
  MakeInternals = false
  MapMode = 5
  sketch-geometry (1):
    g0: Circle CenterX=-36.8843 CenterY=-31.8769 CenterZ=0 NormalX=0 NormalY=0 NormalZ=1 AngleXU=0 Radius=1
  constraints (1):
    c: Diameter(g0) = 2
FEATURE [PartDesign::Pad] Pad040
  Direction = (0,0,1)
  Length = 10
  Length2 = 10
  Profile = -> Sketch040
  ReferenceAxis = -> Sketch040 [N_Axis]
  Refine = true
  Suppressed = false
  Type = 0
FEATURE [PartDesign::Body] Body040
  AllowCompound = false
  Group = -> [Sketch040,Pad040]
  Origin = -> Origin040
  Placement = pos=(-82,35,-4) rot=(0,0,1;0rad)
  Tip = -> Pad040
FEATURE [Sketcher::SketchObject] Sketch041
  ArcFitTolerance = 1e-06
  AttachmentSupport = -> [XY_Plane041]
  FullyConstrained = false
  MakeInternals = false
  MapMode = 5
  sketch-geometry (1):
    g0: Circle CenterX=-36.8843 CenterY=-31.8769 CenterZ=0 NormalX=0 NormalY=0 NormalZ=1 AngleXU=0 Radius=1
  constraints (1):
    c: Diameter(g0) = 2
FEATURE [PartDesign::Pad] Pad041
  Direction = (0,0,1)
  Length = 10
  Length2 = 10
  Profile = -> Sketch041
  ReferenceAxis = -> Sketch041 [N_Axis]
  Refine = true
  Suppressed = false
  Type = 0
FEATURE [PartDesign::Body] Body041
  AllowCompound = false
  Group = -> [Sketch041,Pad041]
  Origin = -> Origin041
  Placement = pos=(-77,35,-4) rot=(0,0,1;0rad)
  Tip = -> Pad041
FEATURE [PartDesign::Boolean] Boolean008
  BaseFeature = -> Boolean007
  Group = -> [Body036,Body037,Body038,Body039,Body040,Body041]
  Refine = true
  Suppressed = false
  Type = 1
  UsePlacement = true
FEATURE [Sketcher::SketchObject] Sketch042
  ArcFitTolerance = 1e-06
  AttachmentSupport = -> [XY_Plane042]
  FullyConstrained = false
  MakeInternals = false
  MapMode = 5
  sketch-geometry (1):
    g0: Circle CenterX=-36.8843 CenterY=-31.8769 CenterZ=0 NormalX=0 NormalY=0 NormalZ=1 AngleXU=0 Radius=1
  constraints (1):
    c: Diameter(g0) = 2
FEATURE [PartDesign::Pad] Pad042
  Direction = (0,0,1)
  Length = 10
  Length2 = 10
  Profile = -> Sketch042
  ReferenceAxis = -> Sketch042 [N_Axis]
  Refine = true
  Suppressed = false
  Type = 0
FEATURE [PartDesign::Body] Body042
  AllowCompound = false
  Group = -> [Sketch042,Pad042]
  Origin = -> Origin042
  Placement = pos=(-102,39,-4) rot=(0,0,1;0rad)
  Tip = -> Pad042
FEATURE [Sketcher::SketchObject] Sketch043
  ArcFitTolerance = 1e-06
  AttachmentSupport = -> [XY_Plane043]
  FullyConstrained = false
  MakeInternals = false
  MapMode = 5
  sketch-geometry (1):
    g0: Circle CenterX=-36.8843 CenterY=-31.8769 CenterZ=0 NormalX=0 NormalY=0 NormalZ=1 AngleXU=0 Radius=1
  constraints (1):
    c: Diameter(g0) = 2
FEATURE [PartDesign::Pad] Pad043
  Direction = (0,0,1)
  Length = 10
  Length2 = 10
  Profile = -> Sketch043
  ReferenceAxis = -> Sketch043 [N_Axis]
  Refine = true
  Suppressed = false
  Type = 0
FEATURE [PartDesign::Body] Body043
  AllowCompound = false
  Group = -> [Sketch043,Pad043]
  Origin = -> Origin043
  Placement = pos=(-97,39,-4) rot=(0,0,1;0rad)
  Tip = -> Pad043
FEATURE [Sketcher::SketchObject] Sketch044
  ArcFitTolerance = 1e-06
  AttachmentSupport = -> [XY_Plane044]
  FullyConstrained = false
  MakeInternals = false
  MapMode = 5
  sketch-geometry (1):
    g0: Circle CenterX=-36.8843 CenterY=-31.8769 CenterZ=0 NormalX=0 NormalY=0 NormalZ=1 AngleXU=0 Radius=1
  constraints (1):
    c: Diameter(g0) = 2
FEATURE [PartDesign::Pad] Pad044
  Direction = (0,0,1)
  Length = 10
  Length2 = 10
  Profile = -> Sketch044
  ReferenceAxis = -> Sketch044 [N_Axis]
  Refine = true
  Suppressed = false
  Type = 0
FEATURE [PartDesign::Body] Body044
  AllowCompound = false
  Group = -> [Sketch044,Pad044]
  Origin = -> Origin044
  Placement = pos=(-92,39,-4) rot=(0,0,1;0rad)
  Tip = -> Pad044
FEATURE [Sketcher::SketchObject] Sketch045
  ArcFitTolerance = 1e-06
  AttachmentSupport = -> [XY_Plane045]
  FullyConstrained = false
  MakeInternals = false
  MapMode = 5
  sketch-geometry (1):
    g0: Circle CenterX=-36.8843 CenterY=-31.8769 CenterZ=0 NormalX=0 NormalY=0 NormalZ=1 AngleXU=0 Radius=1
  constraints (1):
    c: Diameter(g0) = 2
FEATURE [PartDesign::Pad] Pad045
  Direction = (0,0,1)
  Length = 10
  Length2 = 10
  Profile = -> Sketch045
  ReferenceAxis = -> Sketch045 [N_Axis]
  Refine = true
  Suppressed = false
  Type = 0
FEATURE [PartDesign::Body] Body045
  AllowCompound = false
  Group = -> [Sketch045,Pad045]
  Origin = -> Origin045
  Placement = pos=(-87,39,-4) rot=(0,0,1;0rad)
  Tip = -> Pad045
FEATURE [Sketcher::SketchObject] Sketch046
  ArcFitTolerance = 1e-06
  AttachmentSupport = -> [XY_Plane046]
  FullyConstrained = false
  MakeInternals = false
  MapMode = 5
  sketch-geometry (1):
    g0: Circle CenterX=-36.8843 CenterY=-31.8769 CenterZ=0 NormalX=0 NormalY=0 NormalZ=1 AngleXU=0 Radius=1
  constraints (1):
    c: Diameter(g0) = 2
FEATURE [PartDesign::Pad] Pad046
  Direction = (0,0,1)
  Length = 10
  Length2 = 10
  Profile = -> Sketch046
  ReferenceAxis = -> Sketch046 [N_Axis]
  Refine = true
  Suppressed = false
  Type = 0
FEATURE [PartDesign::Body] Body046
  AllowCompound = false
  Group = -> [Sketch046,Pad046]
  Origin = -> Origin046
  Placement = pos=(-82,39,-4) rot=(0,0,1;0rad)
  Tip = -> Pad046
FEATURE [Sketcher::SketchObject] Sketch047
  ArcFitTolerance = 1e-06
  AttachmentSupport = -> [XY_Plane047]
  FullyConstrained = false
  MakeInternals = false
  MapMode = 5
  sketch-geometry (1):
    g0: Circle CenterX=-36.8843 CenterY=-31.8769 CenterZ=0 NormalX=0 NormalY=0 NormalZ=1 AngleXU=0 Radius=1
  constraints (1):
    c: Diameter(g0) = 2
FEATURE [PartDesign::Pad] Pad047
  Direction = (0,0,1)
  Length = 10
  Length2 = 10
  Profile = -> Sketch047
  ReferenceAxis = -> Sketch047 [N_Axis]
  Refine = true
  Suppressed = false
  Type = 0
FEATURE [PartDesign::Body] Body047
  AllowCompound = false
  Group = -> [Sketch047,Pad047]
  Origin = -> Origin047
  Placement = pos=(-77,39,-4) rot=(0,0,1;0rad)
  Tip = -> Pad047
FEATURE [PartDesign::Boolean] Boolean009
  BaseFeature = -> Boolean008
  Group = -> [Body042,Body043,Body044,Body045,Body046,Body047]
  Refine = true
  Suppressed = false
  Type = 1
  UsePlacement = true
FEATURE [Sketcher::SketchObject] Sketch048
  ArcFitTolerance = 1e-06
  AttachmentSupport = -> [XY_Plane048]
  FullyConstrained = false
  MakeInternals = false
  MapMode = 5
  sketch-geometry (1):
    g0: Circle CenterX=-36.8843 CenterY=-31.8769 CenterZ=0 NormalX=0 NormalY=0 NormalZ=1 AngleXU=0 Radius=1
  constraints (1):
    c: Diameter(g0) = 2
FEATURE [PartDesign::Pad] Pad048
  Direction = (0,0,1)
  Length = 10
  Length2 = 10
  Profile = -> Sketch048
  ReferenceAxis = -> Sketch048 [N_Axis]
  Refine = true
  Suppressed = false
  Type = 0
FEATURE [PartDesign::Body] Body048
  AllowCompound = false
  Group = -> [Sketch048,Pad048]
  Origin = -> Origin048
  Placement = pos=(-102,43,-4) rot=(0,0,1;0rad)
  Tip = -> Pad048
FEATURE [Sketcher::SketchObject] Sketch049
  ArcFitTolerance = 1e-06
  AttachmentSupport = -> [XY_Plane049]
  FullyConstrained = false
  MakeInternals = false
  MapMode = 5
  sketch-geometry (1):
    g0: Circle CenterX=-36.8843 CenterY=-31.8769 CenterZ=0 NormalX=0 NormalY=0 NormalZ=1 AngleXU=0 Radius=1
  constraints (1):
    c: Diameter(g0) = 2
FEATURE [PartDesign::Pad] Pad049
  Direction = (0,0,1)
  Length = 10
  Length2 = 10
  Profile = -> Sketch049
  ReferenceAxis = -> Sketch049 [N_Axis]
  Refine = true
  Suppressed = false
  Type = 0
FEATURE [PartDesign::Body] Body049
  AllowCompound = false
  Group = -> [Sketch049,Pad049]
  Origin = -> Origin049
  Placement = pos=(-97,43,-4) rot=(0,0,1;0rad)
  Tip = -> Pad049
FEATURE [Sketcher::SketchObject] Sketch050
  ArcFitTolerance = 1e-06
  AttachmentSupport = -> [XY_Plane050]
  FullyConstrained = false
  MakeInternals = false
  MapMode = 5
  sketch-geometry (1):
    g0: Circle CenterX=-36.8843 CenterY=-31.8769 CenterZ=0 NormalX=0 NormalY=0 NormalZ=1 AngleXU=0 Radius=1
  constraints (1):
    c: Diameter(g0) = 2
FEATURE [PartDesign::Pad] Pad050
  Direction = (0,0,1)
  Length = 10
  Length2 = 10
  Profile = -> Sketch050
  ReferenceAxis = -> Sketch050 [N_Axis]
  Refine = true
  Suppressed = false
  Type = 0
FEATURE [PartDesign::Body] Body050
  AllowCompound = false
  Group = -> [Sketch050,Pad050]
  Origin = -> Origin050
  Placement = pos=(-92,43,-4) rot=(0,0,1;0rad)
  Tip = -> Pad050
FEATURE [Sketcher::SketchObject] Sketch051
  ArcFitTolerance = 1e-06
  AttachmentSupport = -> [XY_Plane051]
  FullyConstrained = false
  MakeInternals = false
  MapMode = 5
  sketch-geometry (1):
    g0: Circle CenterX=-36.8843 CenterY=-31.8769 CenterZ=0 NormalX=0 NormalY=0 NormalZ=1 AngleXU=0 Radius=1
  constraints (1):
    c: Diameter(g0) = 2
FEATURE [PartDesign::Pad] Pad051
  Direction = (0,0,1)
  Length = 10
  Length2 = 10
  Profile = -> Sketch051
  ReferenceAxis = -> Sketch051 [N_Axis]
  Refine = true
  Suppressed = false
  Type = 0
FEATURE [PartDesign::Body] Body051
  AllowCompound = false
  Group = -> [Sketch051,Pad051]
  Origin = -> Origin051
  Placement = pos=(-87,43,-4) rot=(0,0,1;0rad)
  Tip = -> Pad051
FEATURE [Sketcher::SketchObject] Sketch052
  ArcFitTolerance = 1e-06
  AttachmentSupport = -> [XY_Plane052]
  FullyConstrained = false
  MakeInternals = false
  MapMode = 5
  sketch-geometry (1):
    g0: Circle CenterX=-36.8843 CenterY=-31.8769 CenterZ=0 NormalX=0 NormalY=0 NormalZ=1 AngleXU=0 Radius=1
  constraints (1):
    c: Diameter(g0) = 2
FEATURE [PartDesign::Pad] Pad052
  Direction = (0,0,1)
  Length = 10
  Length2 = 10
  Profile = -> Sketch052
  ReferenceAxis = -> Sketch052 [N_Axis]
  Refine = true
  Suppressed = false
  Type = 0
FEATURE [PartDesign::Body] Body052
  AllowCompound = false
  Group = -> [Sketch052,Pad052]
  Origin = -> Origin052
  Placement = pos=(-82,43,-4) rot=(0,0,1;0rad)
  Tip = -> Pad052
FEATURE [Sketcher::SketchObject] Sketch053
  ArcFitTolerance = 1e-06
  AttachmentSupport = -> [XY_Plane053]
  FullyConstrained = false
  MakeInternals = false
  MapMode = 5
  sketch-geometry (1):
    g0: Circle CenterX=-36.8843 CenterY=-31.8769 CenterZ=0 NormalX=0 NormalY=0 NormalZ=1 AngleXU=0 Radius=1
  constraints (1):
    c: Diameter(g0) = 2
FEATURE [PartDesign::Pad] Pad053
  Direction = (0,0,1)
  Length = 10
  Length2 = 10
  Profile = -> Sketch053
  ReferenceAxis = -> Sketch053 [N_Axis]
  Refine = true
  Suppressed = false
  Type = 0
FEATURE [PartDesign::Body] Body053
  AllowCompound = false
  Group = -> [Sketch053,Pad053]
  Origin = -> Origin053
  Placement = pos=(-77,43,-4) rot=(0,0,1;0rad)
  Tip = -> Pad053
FEATURE [PartDesign::Boolean] Boolean010
  BaseFeature = -> Boolean009
  Group = -> [Body048,Body049,Body050,Body051,Body052,Body053]
  Refine = true
  Suppressed = false
  Type = 1
  UsePlacement = true
FEATURE [Sketcher::SketchObject] Sketch054
  ArcFitTolerance = 1e-06
  AttachmentSupport = -> [XY_Plane054]
  FullyConstrained = false
  MakeInternals = false
  MapMode = 5
  sketch-geometry (1):
    g0: Circle CenterX=-36.8843 CenterY=-31.8769 CenterZ=0 NormalX=0 NormalY=0 NormalZ=1 AngleXU=0 Radius=1
  constraints (1):
    c: Diameter(g0) = 2
FEATURE [PartDesign::Pad] Pad054
  Direction = (0,0,1)
  Length = 10
  Length2 = 10
  Profile = -> Sketch054
  ReferenceAxis = -> Sketch054 [N_Axis]
  Refine = true
  Suppressed = false
  Type = 0
FEATURE [PartDesign::Body] Body054
  AllowCompound = false
  Group = -> [Sketch054,Pad054]
  Origin = -> Origin054
  Placement = pos=(-102,47,-4) rot=(0,0,1;0rad)
  Tip = -> Pad054
FEATURE [Sketcher::SketchObject] Sketch055
  ArcFitTolerance = 1e-06
  AttachmentSupport = -> [XY_Plane055]
  FullyConstrained = false
  MakeInternals = false
  MapMode = 5
  sketch-geometry (1):
    g0: Circle CenterX=-36.8843 CenterY=-31.8769 CenterZ=0 NormalX=0 NormalY=0 NormalZ=1 AngleXU=0 Radius=1
  constraints (1):
    c: Diameter(g0) = 2
FEATURE [PartDesign::Pad] Pad055
  Direction = (0,0,1)
  Length = 10
  Length2 = 10
  Profile = -> Sketch055
  ReferenceAxis = -> Sketch055 [N_Axis]
  Refine = true
  Suppressed = false
  Type = 0
FEATURE [PartDesign::Body] Body055
  AllowCompound = false
  Group = -> [Sketch055,Pad055]
  Origin = -> Origin055
  Placement = pos=(-97,47,-4) rot=(0,0,1;0rad)
  Tip = -> Pad055
FEATURE [Sketcher::SketchObject] Sketch056
  ArcFitTolerance = 1e-06
  AttachmentSupport = -> [XY_Plane056]
  FullyConstrained = false
  MakeInternals = false
  MapMode = 5
  sketch-geometry (1):
    g0: Circle CenterX=-36.8843 CenterY=-31.8769 CenterZ=0 NormalX=0 NormalY=0 NormalZ=1 AngleXU=0 Radius=1
  constraints (1):
    c: Diameter(g0) = 2
FEATURE [PartDesign::Pad] Pad056
  Direction = (0,0,1)
  Length = 10
  Length2 = 10
  Profile = -> Sketch056
  ReferenceAxis = -> Sketch056 [N_Axis]
  Refine = true
  Suppressed = false
  Type = 0
FEATURE [PartDesign::Body] Body056
  AllowCompound = false
  Group = -> [Sketch056,Pad056]
  Origin = -> Origin056
  Placement = pos=(-92,47,-4) rot=(0,0,1;0rad)
  Tip = -> Pad056
FEATURE [Sketcher::SketchObject] Sketch057
  ArcFitTolerance = 1e-06
  AttachmentSupport = -> [XY_Plane057]
  FullyConstrained = false
  MakeInternals = false
  MapMode = 5
  sketch-geometry (1):
    g0: Circle CenterX=-36.8843 CenterY=-31.8769 CenterZ=0 NormalX=0 NormalY=0 NormalZ=1 AngleXU=0 Radius=1
  constraints (1):
    c: Diameter(g0) = 2
FEATURE [PartDesign::Pad] Pad057
  Direction = (0,0,1)
  Length = 10
  Length2 = 10
  Profile = -> Sketch057
  ReferenceAxis = -> Sketch057 [N_Axis]
  Refine = true
  Suppressed = false
  Type = 0
FEATURE [PartDesign::Body] Body057
  AllowCompound = false
  Group = -> [Sketch057,Pad057]
  Origin = -> Origin057
  Placement = pos=(-87,47,-4) rot=(0,0,1;0rad)
  Tip = -> Pad057
FEATURE [Sketcher::SketchObject] Sketch058
  ArcFitTolerance = 1e-06
  AttachmentSupport = -> [XY_Plane058]
  FullyConstrained = false
  MakeInternals = false
  MapMode = 5
  sketch-geometry (1):
    g0: Circle CenterX=-36.8843 CenterY=-31.8769 CenterZ=0 NormalX=0 NormalY=0 NormalZ=1 AngleXU=0 Radius=1
  constraints (1):
    c: Diameter(g0) = 2
FEATURE [PartDesign::Pad] Pad058
  Direction = (0,0,1)
  Length = 10
  Length2 = 10
  Profile = -> Sketch058
  ReferenceAxis = -> Sketch058 [N_Axis]
  Refine = true
  Suppressed = false
  Type = 0
FEATURE [PartDesign::Body] Body058
  AllowCompound = false
  Group = -> [Sketch058,Pad058]
  Origin = -> Origin058
  Placement = pos=(-82,47,-4) rot=(0,0,1;0rad)
  Tip = -> Pad058
FEATURE [Sketcher::SketchObject] Sketch059
  ArcFitTolerance = 1e-06
  AttachmentSupport = -> [XY_Plane059]
  FullyConstrained = false
  MakeInternals = false
  MapMode = 5
  sketch-geometry (1):
    g0: Circle CenterX=-36.8843 CenterY=-31.8769 CenterZ=0 NormalX=0 NormalY=0 NormalZ=1 AngleXU=0 Radius=1
  constraints (1):
    c: Diameter(g0) = 2
FEATURE [PartDesign::Pad] Pad059
  Direction = (0,0,1)
  Length = 10
  Length2 = 10
  Profile = -> Sketch059
  ReferenceAxis = -> Sketch059 [N_Axis]
  Refine = true
  Suppressed = false
  Type = 0
FEATURE [PartDesign::Body] Body059
  AllowCompound = false
  Group = -> [Sketch059,Pad059]
  Origin = -> Origin059
  Placement = pos=(-77,47,-4) rot=(0,0,1;0rad)
  Tip = -> Pad059
FEATURE [PartDesign::Boolean] Boolean011
  BaseFeature = -> Boolean010
  Group = -> [Body054,Body055,Body056,Body057,Body058,Body059]
  Refine = true
  Suppressed = false
  Type = 1
  UsePlacement = true
FEATURE [Sketcher::SketchObject] Sketch060
  ArcFitTolerance = 1e-06
  AttachmentSupport = -> [XY_Plane060]
  FullyConstrained = false
  MakeInternals = false
  MapMode = 5
  sketch-geometry (1):
    g0: Circle CenterX=-36.8843 CenterY=-31.8769 CenterZ=0 NormalX=0 NormalY=0 NormalZ=1 AngleXU=0 Radius=1
  constraints (1):
    c: Diameter(g0) = 2
FEATURE [PartDesign::Pad] Pad060
  Direction = (0,0,1)
  Length = 10
  Length2 = 10
  Profile = -> Sketch060
  ReferenceAxis = -> Sketch060 [N_Axis]
  Refine = true
  Suppressed = false
  Type = 0
FEATURE [PartDesign::Body] Body060
  AllowCompound = false
  Group = -> [Sketch060,Pad060]
  Origin = -> Origin060
  Placement = pos=(-102,51,-4) rot=(0,0,1;0rad)
  Tip = -> Pad060
FEATURE [Sketcher::SketchObject] Sketch061
  ArcFitTolerance = 1e-06
  AttachmentSupport = -> [XY_Plane061]
  FullyConstrained = false
  MakeInternals = false
  MapMode = 5
  sketch-geometry (1):
    g0: Circle CenterX=-36.8843 CenterY=-31.8769 CenterZ=0 NormalX=0 NormalY=0 NormalZ=1 AngleXU=0 Radius=1
  constraints (1):
    c: Diameter(g0) = 2
FEATURE [PartDesign::Pad] Pad061
  Direction = (0,0,1)
  Length = 10
  Length2 = 10
  Profile = -> Sketch061
  ReferenceAxis = -> Sketch061 [N_Axis]
  Refine = true
  Suppressed = false
  Type = 0
FEATURE [PartDesign::Body] Body061
  AllowCompound = false
  Group = -> [Sketch061,Pad061]
  Origin = -> Origin061
  Placement = pos=(-97,51,-4) rot=(0,0,1;0rad)
  Tip = -> Pad061
FEATURE [Sketcher::SketchObject] Sketch062
  ArcFitTolerance = 1e-06
  AttachmentSupport = -> [XY_Plane062]
  FullyConstrained = false
  MakeInternals = false
  MapMode = 5
  sketch-geometry (1):
    g0: Circle CenterX=-36.8843 CenterY=-31.8769 CenterZ=0 NormalX=0 NormalY=0 NormalZ=1 AngleXU=0 Radius=1
  constraints (1):
    c: Diameter(g0) = 2
FEATURE [PartDesign::Pad] Pad062
  Direction = (0,0,1)
  Length = 10
  Length2 = 10
  Profile = -> Sketch062
  ReferenceAxis = -> Sketch062 [N_Axis]
  Refine = true
  Suppressed = false
  Type = 0
FEATURE [PartDesign::Body] Body062
  AllowCompound = false
  Group = -> [Sketch062,Pad062]
  Origin = -> Origin062
  Placement = pos=(-92,51,-4) rot=(0,0,1;0rad)
  Tip = -> Pad062
FEATURE [Sketcher::SketchObject] Sketch063
  ArcFitTolerance = 1e-06
  AttachmentSupport = -> [XY_Plane063]
  FullyConstrained = false
  MakeInternals = false
  MapMode = 5
  sketch-geometry (1):
    g0: Circle CenterX=-36.8843 CenterY=-31.8769 CenterZ=0 NormalX=0 NormalY=0 NormalZ=1 AngleXU=0 Radius=1
  constraints (1):
    c: Diameter(g0) = 2
FEATURE [PartDesign::Pad] Pad063
  Direction = (0,0,1)
  Length = 10
  Length2 = 10
  Profile = -> Sketch063
  ReferenceAxis = -> Sketch063 [N_Axis]
  Refine = true
  Suppressed = false
  Type = 0
FEATURE [PartDesign::Body] Body063
  AllowCompound = false
  Group = -> [Sketch063,Pad063]
  Origin = -> Origin063
  Placement = pos=(-87,51,-4) rot=(0,0,1;0rad)
  Tip = -> Pad063
FEATURE [Sketcher::SketchObject] Sketch064
  ArcFitTolerance = 1e-06
  AttachmentSupport = -> [XY_Plane064]
  FullyConstrained = false
  MakeInternals = false
  MapMode = 5
  sketch-geometry (1):
    g0: Circle CenterX=-36.8843 CenterY=-31.8769 CenterZ=0 NormalX=0 NormalY=0 NormalZ=1 AngleXU=0 Radius=1
  constraints (1):
    c: Diameter(g0) = 2
FEATURE [PartDesign::Pad] Pad064
  Direction = (0,0,1)
  Length = 10
  Length2 = 10
  Profile = -> Sketch064
  ReferenceAxis = -> Sketch064 [N_Axis]
  Refine = true
  Suppressed = false
  Type = 0
FEATURE [PartDesign::Body] Body064
  AllowCompound = false
  Group = -> [Sketch064,Pad064]
  Origin = -> Origin064
  Placement = pos=(-82,51,-4) rot=(0,0,1;0rad)
  Tip = -> Pad064
FEATURE [Sketcher::SketchObject] Sketch065
  ArcFitTolerance = 1e-06
  AttachmentSupport = -> [XY_Plane065]
  FullyConstrained = false
  MakeInternals = false
  MapMode = 5
  sketch-geometry (1):
    g0: Circle CenterX=-36.8843 CenterY=-31.8769 CenterZ=0 NormalX=0 NormalY=0 NormalZ=1 AngleXU=0 Radius=1
  constraints (1):
    c: Diameter(g0) = 2
FEATURE [PartDesign::Pad] Pad065
  Direction = (0,0,1)
  Length = 10
  Length2 = 10
  Profile = -> Sketch065
  ReferenceAxis = -> Sketch065 [N_Axis]
  Refine = true
  Suppressed = false
  Type = 0
FEATURE [PartDesign::Body] Body065
  AllowCompound = false
  Group = -> [Sketch065,Pad065]
  Origin = -> Origin065
  Placement = pos=(-77,51,-4) rot=(0,0,1;0rad)
  Tip = -> Pad065
FEATURE [PartDesign::Boolean] Boolean012
  BaseFeature = -> Boolean011
  Group = -> [Body060,Body061,Body062,Body063,Body064,Body065]
  Refine = true
  Suppressed = false
  Type = 1
  UsePlacement = true
FEATURE [Sketcher::SketchObject] Sketch066
  ArcFitTolerance = 1e-06
  AttachmentSupport = -> [XY_Plane066]
  FullyConstrained = false
  MakeInternals = false
  MapMode = 5
  sketch-geometry (4):
    g0: LineSegment StartX=-100.687 StartY=22.4992 StartZ=0 EndX=-100.687 EndY=-28.5008 EndZ=0
    g1: LineSegment StartX=-100.687 StartY=22.4992 StartZ=0 EndX=-41.1104 EndY=22.4992 EndZ=0
    g2: LineSegment StartX=-41.1104 StartY=22.4992 StartZ=0 EndX=-41.1104 EndY=-28.5008 EndZ=0
    g3: LineSegment StartX=-41.1104 StartY=-28.5008 StartZ=0 EndX=-100.687 EndY=-28.5008 EndZ=0
  constraints (10):
    c: Distance(g0) = 51
    c: Vertical(g0)
    c: PointOnObject(g1,g0)
    c: Horizontal(g1)
    c: Distance(g2) = 51
    c: Coincident(g2,g1)
    c: Vertical(g2)
    c: Coincident(g3,g2)
    c: Coincident(g3,g0)
    c: Horizontal(g3)
FEATURE [PartDesign::Pad] Pad066
  Direction = (0,0,1)
  Length = 10
  Length2 = 10
  Profile = -> Sketch066
  ReferenceAxis = -> Sketch066 [N_Axis]
  Refine = true
  Suppressed = false
  Type = 0
FEATURE [PartDesign::Body] Body066
  AllowCompound = false
  Group = -> [Sketch066,Pad066]
  Origin = -> Origin066
  Placement = pos=(-5,5,0) rot=(0,0,1;0rad)
  Tip = -> Pad066
FEATURE [PartDesign::Boolean] Boolean013
  BaseFeature = -> Boolean012
  Group = -> [Body066]
  Refine = true
  Suppressed = false
  Type = 1
  UsePlacement = true
FEATURE [PartDesign::Body] Body004
  AllowCompound = false
  Group = -> [Sketch004,Pad004,Boolean003,Boolean004,Boolean005,Boolean006,Boolean007,Boolean008,Boolean009,Boolean010,Boolean011,Boolean012,Boolean013]
  Origin = -> Origin004
  Placement = pos=(54,0,0) rot=(0,0,1;0rad)
  Tip = -> Boolean013
